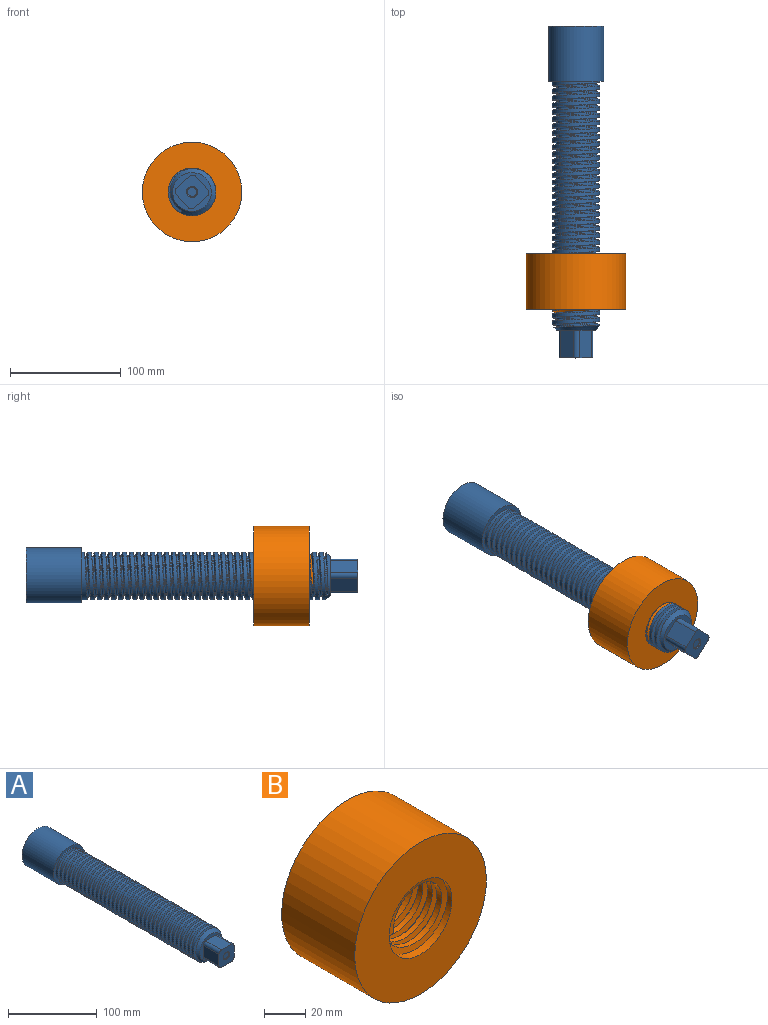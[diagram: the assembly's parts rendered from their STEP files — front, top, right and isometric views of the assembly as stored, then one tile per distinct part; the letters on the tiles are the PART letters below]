
ASSEMBLY  parts=2 mates=1
PART A: 22 faces, bbox 50x300x50.1 mm
  f0: cylinder r=21.5mm len=221mm, axis (0,-1,0), area 15002.6mm2, adj f1,f4,f12,f13,f14
  f1: cone r=17.5mm half-angle=45deg, axis (0,1,0), area 581.5mm2, adj f0,f9,f11,f14
  f2: cylinder r=25mm len=50mm, axis (0,1,0), area 7854mm2, adj f3,f4
  f3: plane 50x50mm, normal (0,1,0), area 1963.5mm2, adj f2
  f4: plane 50.02x50.02mm, normal (0,-1,0), area 511.3mm2, adj f0,f2,f13
  f5: plane 25x16mm, normal (1,0,0), area 400mm2, adj f9,f10,f16,f19
  f6: plane 25x16mm, normal (0,0,-1), area 400mm2, adj f9,f10,f16,f17
  f7: plane 25x16mm, normal (-1,0,0), area 400mm2, adj f9,f10,f17,f18
  f8: plane 25x16mm, normal (0,0,1), area 400mm2, adj f9,f10,f18,f19
  f9: plane 35x35mm, normal (0,-1,0), area 399.8mm2, adj f1,f5,f6,f7,f8,f16,f17,f18
  f10: plane 24x24mm, normal (0,-1,0), area 483.7mm2, adj f5,f6,f7,f8,f16,f17,f18,f19
  f11: plane 3.14x2.43mm, normal (-0.94,0,-0.33), area 3.8mm2, adj f1,f13,f14,f15
  f12: plane 3.34x3.19mm, normal (0,0,1), area 7.7mm2, adj f0,f13,f14,f15
  f13: bspline ~221.89x48.76mm, area 14739.1mm2, adj f0,f4,f11,f12,f15
  f14: bspline ~222.21x48.76mm, area 15004.2mm2, adj f0,f1,f11,f12,f15
  f15: cylinder r=18.18mm len=222.46mm, axis (0,1,0), area 5753.2mm2, adj f11,f12,f13,f14
  f16: cylinder r=4mm len=25mm, axis (0,1,0), area 157.1mm2, adj f5,f6,f9,f10
  f17: cylinder r=4mm len=25mm, axis (0,-1,0), area 157.1mm2, adj f6,f7,f9,f10
  f18: cylinder r=4mm len=25mm, axis (0,1,0), area 157.1mm2, adj f7,f8,f9,f10
  f19: cylinder r=4mm len=25mm, axis (0,-1,0), area 157.1mm2, adj f5,f8,f9,f10
  f20: plane 8x8mm, normal (0,-1,0), area 50.3mm2, adj f21
  f21: cone r=3mm half-angle=45deg, axis (0,-1,0), area 40mm2, adj f10,f20
PART B: 10 faces, bbox 90x54.6x90 mm
  f0: cylinder r=21.5mm len=50mm, axis (0,1,0), area 5359.2mm2, adj f2,f3,f5,f7,f8
  f1: cylinder r=45mm len=90mm, axis (0,1,0), area 14137.2mm2, adj f2,f3
  f2: plane 90x90mm, normal (0,-1,0), area 4909.5mm2, adj f0,f1
  f3: plane 90x90mm, normal (0,1,0), area 4909.5mm2, adj f0,f1,f4
  f4: cylinder r=21.5mm len=34.87mm, axis (0,1,0), area 41.2mm2, adj f3,f6,f7
  f5: plane 3.76x3.4mm, normal (0,0,-1), area 8.8mm2, adj f0,f7,f8,f9
  f6: plane 3.77x2.44mm, normal (-0.71,0,0.7), area 8.8mm2, adj f4,f7,f8,f9
  f7: bspline ~52.59x49.65mm, area 3775.8mm2, adj f0,f4,f5,f6,f9
  f8: bspline ~51.38x49.65mm, area 3367.5mm2, adj f0,f5,f6,f9
  f9: cylinder r=18.1mm len=53.18mm, axis (0,1,0), area 2843.1mm2, adj f5,f6,f7,f8
PLACE A rot(axis=(0,1,0),47.7deg) t=(-78.28,122.64,0)mm
PLACE B rot(axis=(-0.83,0,-0.56),180deg) t=(-78.28,-133.28,0)mm fixed
MATE cylindrical A.f21 <-> B.f0  axis (0,-1,0) through (-78.28,-176.36,0)mm
